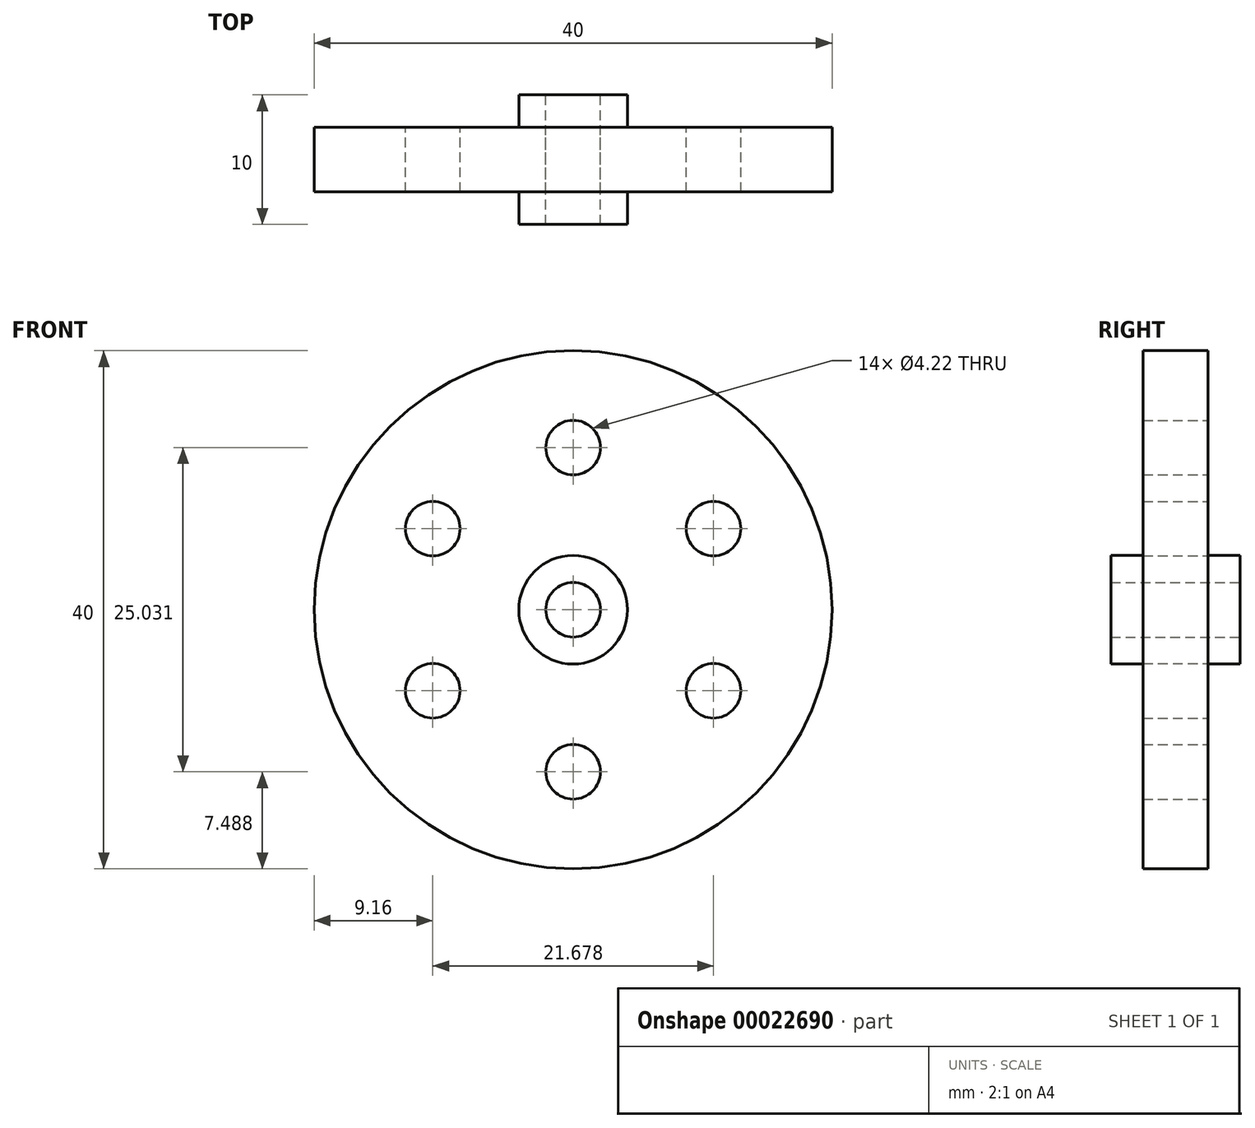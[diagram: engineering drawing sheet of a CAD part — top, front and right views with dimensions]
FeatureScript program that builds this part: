
annotation { "Feature Type Name" : "Feature", "Feature Type Description" : "" }
export const myFeature = defineFeature(function(context is Context, id is Id, definition is map)
    precondition{}
    {
        {
            var Q0;
            Q0=qCreatedBy(makeId("Front.planeOp"),FACE);
            var sketch = newSketch(context, id + "F0", { "sketchPlane" : qUnion([Q0])});
            skCircle(sketch, "E0", {"center": v(-79.86, 35.01) * mm, "radius": 20 * mm});
            skCircle(sketch, "E1", {"center": v(-79.86, 35.01) * mm, "radius": 2.1 * mm});
            skCircle(sketch, "E2", {"center": v(-79.86, 47.53) * mm, "radius": 2.1 * mm});
            skCircle(sketch, "E3.1.0", {"center": v(-90.7, 41.27) * mm, "radius": 2.1 * mm});
            skCircle(sketch, "E3.2.0", {"center": v(-90.7, 28.76) * mm, "radius": 2.1 * mm});
            skCircle(sketch, "E3.3.0", {"center": v(-79.86, 22.5) * mm, "radius": 2.1 * mm});
            skCircle(sketch, "E3.4.0", {"center": v(-69.02, 28.76) * mm, "radius": 2.1 * mm});
            skCircle(sketch, "E3.5.0", {"center": v(-69.02, 41.27) * mm, "radius": 2.1 * mm});
            skCircle(sketch, "E4", {"center": v(-79.86, 35.01) * mm, "radius": 4.2 * mm});
            skSolve(sketch);
        }
        {
            var Q0;
            Q0 = qSketchRegion(id + "F0", true);
            extrude(context, id + "F1", {"entities" : qUnion([Q0]), "endBound" : BoundingType.SYMMETRIC, "depth" : 5 * mm});
        }
        {
            var Q0;
            Q0=makeQuery(id+"F0.imprint","IMPRINT",FACE,{"disambiguationData":[TD([[makeQuery(id+"F0.imprint","IMPRINT",EDGE,{"derivedFrom":sQuery(id+"F0.wireOp",EDGE,"E1")}),-1.0]])]});
            extrude(context, id + "F2", {"entities" : qUnion([Q0]), "operationType" : NewBodyOperationType.ADD, "endBound" : BoundingType.SYMMETRIC, "depth" : 10 * mm});
        }
        {
            var Q0;
            Q0=makeQuery(id+"F1.opExtrude","SWEPT_BODY",BODY,{"disambiguationData":[OSD([sQuery(id+"F0.wireOp",EDGE,"E0"),sQuery(id+"F0.wireOp",EDGE,"E2"),sQuery(id+"F0.wireOp",EDGE,"E3.1.0"),sQuery(id+"F0.wireOp",EDGE,"E3.2.0"),sQuery(id+"F0.wireOp",EDGE,"E3.3.0"),sQuery(id+"F0.wireOp",EDGE,"E3.4.0"),sQuery(id+"F0.wireOp",EDGE,"E3.5.0"),sQuery(id+"F0.wireOp",EDGE,"E4")])]});
            transform(context, id + "F3", {"entities" : qUnion([Q0]), "transformType" : TransformType.TRANSLATION_3D, "dx" : 0 * mm, "dy" : 0 * mm, "dz" : 0 * mm, "makeCopy" : true});
        }
    });
